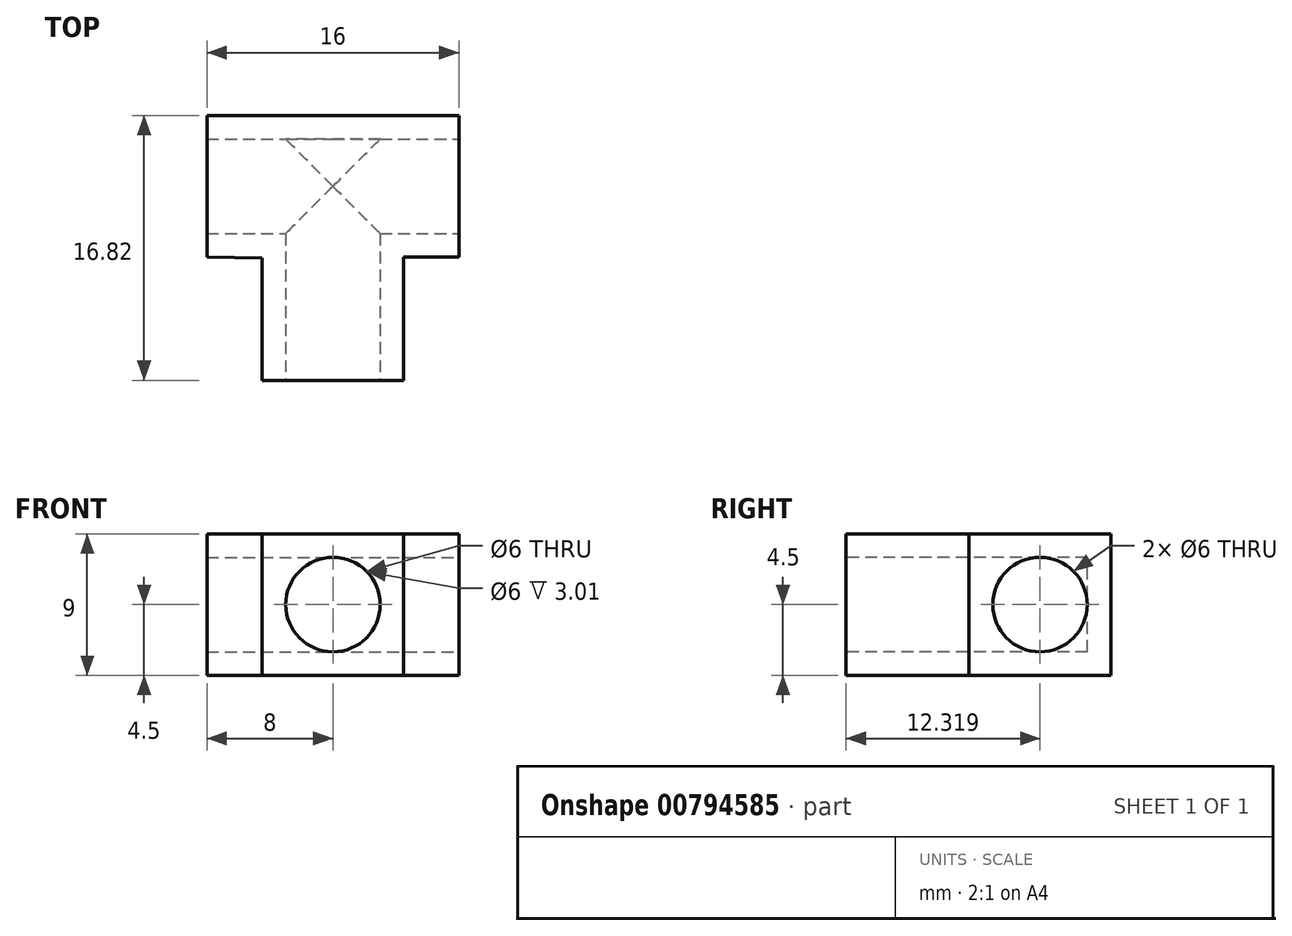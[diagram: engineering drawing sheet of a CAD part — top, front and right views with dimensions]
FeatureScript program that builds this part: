
annotation { "Feature Type Name" : "Feature", "Feature Type Description" : "" }
export const myFeature = defineFeature(function(context is Context, id is Id, definition is map)
    precondition{}
    {
        {
            var Q0;
            Q0=qCreatedBy(makeId("Top.planeOp"),FACE);
            var sketch = newSketch(context, id + "F0", { "sketchPlane" : qUnion([Q0])});
            skLineSegment(sketch, "E0", {"start": v(0, 13.09) * mm, "end": v(8, 13.09) * mm});
            skLineSegment(sketch, "E1", {"start": v(0, 13.09) * mm, "end": v(-8, 13.09) * mm});
            skLineSegment(sketch, "E2", {"start": v(-8, 13.09) * mm, "end": v(-8, 4.09) * mm});
            skLineSegment(sketch, "E3", {"start": v(8, 13.09) * mm, "end": v(8, 4.09) * mm});
            skLineSegment(sketch, "E4", {"start": v(-4.5, -3.73) * mm, "end": v(0, -3.73) * mm});
            skLineSegment(sketch, "E5", {"start": v(0, -3.73) * mm, "end": v(4.5, -3.73) * mm});
            skLineSegment(sketch, "E6", {"start": v(-4.5, -3.73) * mm, "end": v(-4.5, 4.04) * mm});
            skLineSegment(sketch, "E7", {"start": v(-4.5, 4.04) * mm, "end": v(-8, 4.09) * mm});
            skLineSegment(sketch, "E8", {"start": v(4.5, -3.73) * mm, "end": v(4.5, 4.09) * mm});
            skLineSegment(sketch, "E9", {"start": v(4.5, 4.09) * mm, "end": v(8, 4.09) * mm});
            skSolve(sketch);
        }
        {
            var Q0;
            Q0 = qSketchRegion(id + "F0", true);
            extrude(context, id + "F1", {"entities" : qUnion([Q0]), "depth" : 9 * mm, "offsetDistance" : 25 * mm});
        }
        {
            var Q0;
            Q0=makeQuery(id+"F1.opExtrude","SWEPT_FACE",FACE,{"disambiguationData":[OSD([sQuery(id+"F0.wireOp",EDGE,"E4"),sQuery(id+"F0.wireOp",EDGE,"E5")])]});
            var sketch = newSketch(context, id + "F2", { "sketchPlane" : qUnion([Q0])});
            skCircle(sketch, "E10", {"center": v(0, 4.5) * mm, "radius": 3 * mm});
            skSolve(sketch);
        }
        {
            var Q0;
            Q0=makeQuery(id+"F1.opExtrude","SWEPT_FACE",FACE,{"disambiguationData":[OSD([sQuery(id+"F0.wireOp",EDGE,"E3")])]});
            var sketch = newSketch(context, id + "F3", { "sketchPlane" : qUnion([Q0])});
            skCircle(sketch, "E11", {"center": v(8.59, 4.5) * mm, "radius": 3 * mm});
            skPoint(sketch, "E11.centerSnap0", {"position": v(8.59, 9) * mm});
            skSolve(sketch);
        }
        {
            var Q0;
            Q0=makeQuery(id+"F3.imprint","IMPRINT",FACE,{"disambiguationData":[TD([[makeQuery(id+"F3.imprint","IMPRINT",EDGE,{"derivedFrom":sQuery(id+"F3.wireOp",EDGE,"E11")}),1.0]])]});
            extrude(context, id + "F4", {"entities" : qUnion([Q0]), "operationType" : NewBodyOperationType.REMOVE, "oppositeDirection" : true, "depth" : 16 * mm, "offsetDistance" : 25 * mm});
        }
        {
            var Q0;
            Q0=makeQuery(id+"F2.imprint","IMPRINT",FACE,{"disambiguationData":[TD([[makeQuery(id+"F2.imprint","IMPRINT",EDGE,{"derivedFrom":sQuery(id+"F2.wireOp",EDGE,"E10")}),1.0]])]});
            extrude(context, id + "F5", {"entities" : qUnion([Q0]), "operationType" : NewBodyOperationType.REMOVE, "oppositeDirection" : true, "depth" : 15.32 * mm, "offsetDistance" : 25 * mm});
        }
    });
